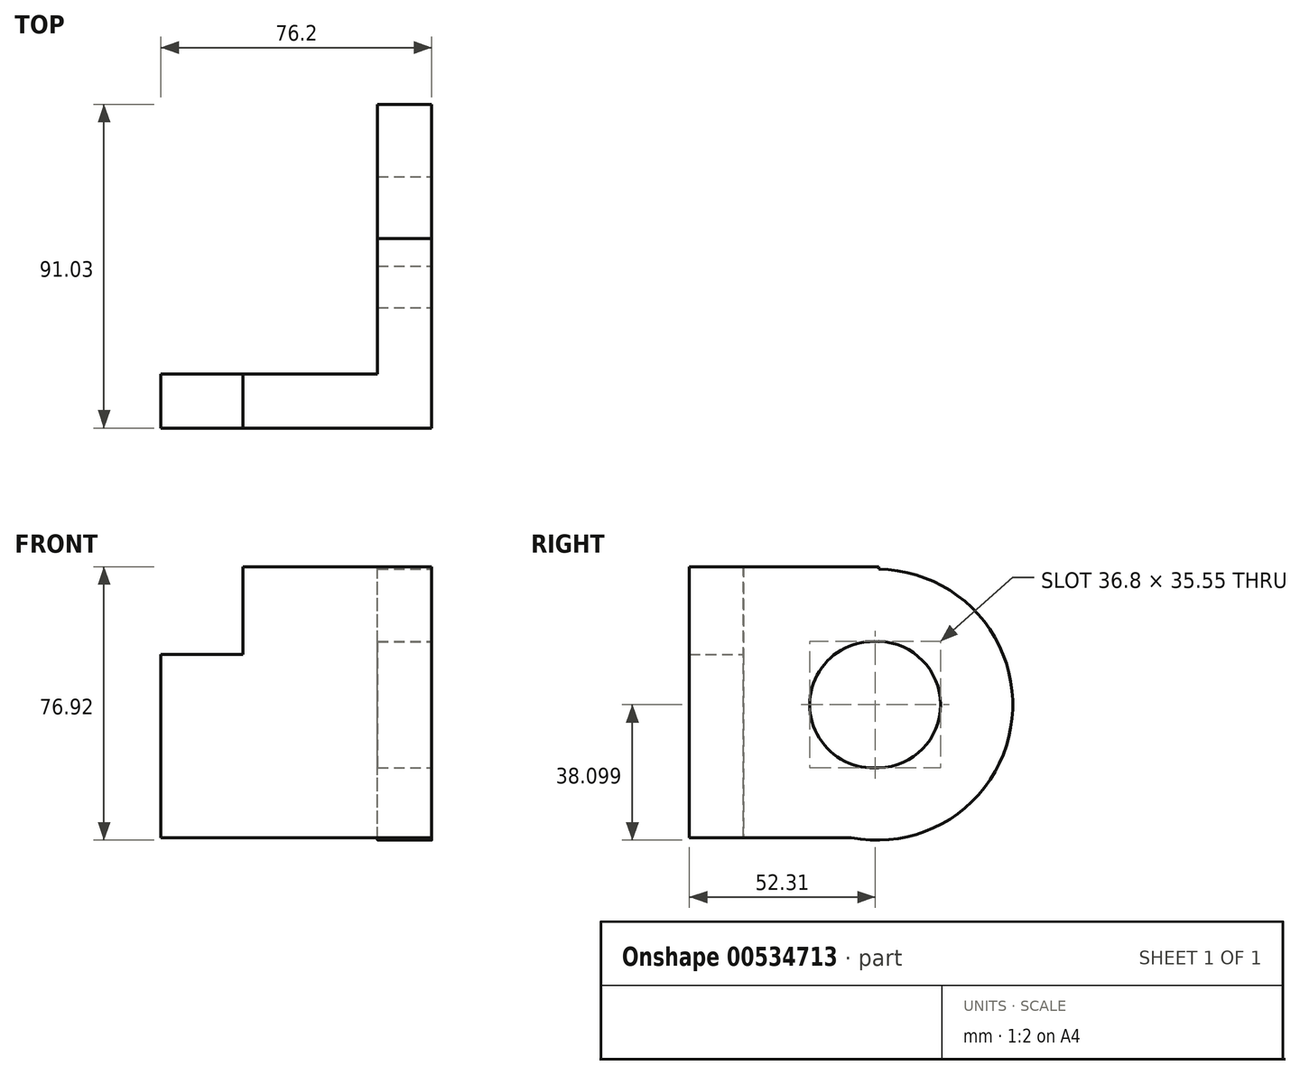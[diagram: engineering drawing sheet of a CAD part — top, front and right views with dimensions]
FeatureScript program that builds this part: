
annotation { "Feature Type Name" : "Feature", "Feature Type Description" : "" }
export const myFeature = defineFeature(function(context is Context, id is Id, definition is map)
    precondition{}
    {
        {
            var Q0;
            Q0=qCreatedBy(makeId("Front.planeOp"),FACE);
            var sketch = newSketch(context, id + "F0", { "sketchPlane" : qUnion([Q0])});
            skLineSegment(sketch, "E0.bottom", {"start": v(-53.13, 76.2) * mm, "end": v(0, 76.2) * mm});
            skLineSegment(sketch, "E0.top", {"start": v(-76.2, 0) * mm, "end": v(0, 0) * mm});
            skLineSegment(sketch, "E0.left", {"start": v(-76.2, 51.59) * mm, "end": v(-76.2, 0) * mm});
            skLineSegment(sketch, "E0.right", {"start": v(0, 76.2) * mm, "end": v(0, 0) * mm});
            skLineSegment(sketch, "E1", {"start": v(-53.13, 76.2) * mm, "end": v(-53.13, 51.59) * mm});
            skLineSegment(sketch, "E2", {"start": v(-53.13, 51.59) * mm, "end": v(-76.2, 51.59) * mm});
            skSolve(sketch);
        }
        {
            var Q0;
            Q0 = qSketchRegion(id + "F0", true);
            extrude(context, id + "F1", {"entities" : qUnion([Q0]), "depth" : 15.24 * mm, "offsetDistance" : 25.4 * mm});
        }
        {
            var Q0;
            Q0=qCreatedBy(makeId("Right.planeOp"),FACE);
            var sketch = newSketch(context, id + "F2", { "sketchPlane" : qUnion([Q0])});
            skCircle(sketch, "E3", {"center": v(37.69, 37.38) * mm, "radius": 38.1 * mm});
            skSolve(sketch);
        }
        {
            var Q0;
            Q0=makeQuery(id+"F2.imprint","IMPRINT",FACE,{"disambiguationData":[TD([[makeQuery(id+"F2.imprint","IMPRINT",EDGE,{"derivedFrom":sQuery(id+"F2.wireOp",EDGE,"E3")}),1.0]])]});
            extrude(context, id + "F3", {"entities" : qUnion([Q0]), "operationType" : NewBodyOperationType.ADD, "oppositeDirection" : true, "depth" : 15.24 * mm, "offsetDistance" : 25.4 * mm});
        }
        {
            var Q0;
            Q0=makeQuery(id+"F3.boolean.opBoolean","MERGE",FACE,{"derivedFrom":[makeQuery(id+"F1.opExtrude","SWEPT_FACE",FACE,{"disambiguationData":[OSD([sQuery(id+"F0.wireOp",EDGE,"E0.right")])]}),makeQuery(id+"F3.opExtrude","CAP_FACE",FACE,{"disambiguationData":[OSD([sQuery(id+"F2.wireOp",EDGE,"E3")])],"isStart":true})]});
            var sketch = newSketch(context, id + "F4", { "sketchPlane" : qUnion([Q0])});
            skCircle(sketch, "E4", {"center": v(37.69, 37.38) * mm, "radius": 17.78 * mm});
            skSolve(sketch);
        }
        {
            var Q0;
            Q0=makeQuery(id+"F4.imprint","IMPRINT",FACE,{"disambiguationData":[TD([[makeQuery(id+"F4.imprint","IMPRINT",EDGE,{"derivedFrom":sQuery(id+"F4.wireOp",EDGE,"E4")}),1.0]])]});
            extrude(context, id + "F5", {"entities" : qUnion([Q0]), "operationType" : NewBodyOperationType.REMOVE, "oppositeDirection" : true, "depth" : 15.24 * mm, "offsetDistance" : 25.4 * mm});
        }
        {
            var Q0;
            Q0=qCreatedBy(makeId("Right.planeOp"),FACE);
            var sketch = newSketch(context, id + "F6", { "sketchPlane" : qUnion([Q0])});
            skLineSegment(sketch, "E5.bottom", {"start": v(0, 76.2) * mm, "end": v(38.1, 76.2) * mm});
            skLineSegment(sketch, "E5.top", {"start": v(0, 0) * mm, "end": v(38.1, 0) * mm});
            skLineSegment(sketch, "E5.left", {"start": v(0, 76.2) * mm, "end": v(0, 0) * mm});
            skLineSegment(sketch, "E5.right", {"start": v(38.1, 76.2) * mm, "end": v(38.1, 0) * mm});
            skSolve(sketch);
        }
        {
            var Q0;
            Q0 = qSketchRegion(id + "F6", true);
            extrude(context, id + "F7", {"entities" : qUnion([Q0]), "operationType" : NewBodyOperationType.ADD, "oppositeDirection" : true, "depth" : 15.24 * mm, "offsetDistance" : 25.4 * mm});
        }
        {
            var Q0;
            Q0=makeQuery(id+"F7.boolean.opBoolean","MERGE",FACE,{"derivedFrom":[makeQuery(id+"F3.boolean.opBoolean","MERGE",FACE,{"derivedFrom":[makeQuery(id+"F1.opExtrude","SWEPT_FACE",FACE,{"disambiguationData":[OSD([sQuery(id+"F0.wireOp",EDGE,"E0.right")])]}),makeQuery(id+"F3.opExtrude","CAP_FACE",FACE,{"disambiguationData":[OSD([sQuery(id+"F2.wireOp",EDGE,"E3")])],"isStart":true})]}),makeQuery(id+"F7.opExtrude","CAP_FACE",FACE,{"disambiguationData":[OSD([sQuery(id+"F6.wireOp",EDGE,"E5.bottom"),sQuery(id+"F6.wireOp",EDGE,"E5.top"),sQuery(id+"F6.wireOp",EDGE,"E5.left"),sQuery(id+"F6.wireOp",EDGE,"E5.right")])],"isStart":true})]});
            var sketch = newSketch(context, id + "F8", { "sketchPlane" : qUnion([Q0])});
            skCircle(sketch, "E6", {"center": v(36.45, 37.38) * mm, "radius": 17.78 * mm});
            skSolve(sketch);
        }
        {
            var Q0;
            Q0 = qSketchRegion(id + "F8", true);
            extrude(context, id + "F9", {"entities" : qUnion([Q0]), "operationType" : NewBodyOperationType.REMOVE, "oppositeDirection" : true, "depth" : 15.24 * mm, "offsetDistance" : 25.4 * mm});
        }
    });
